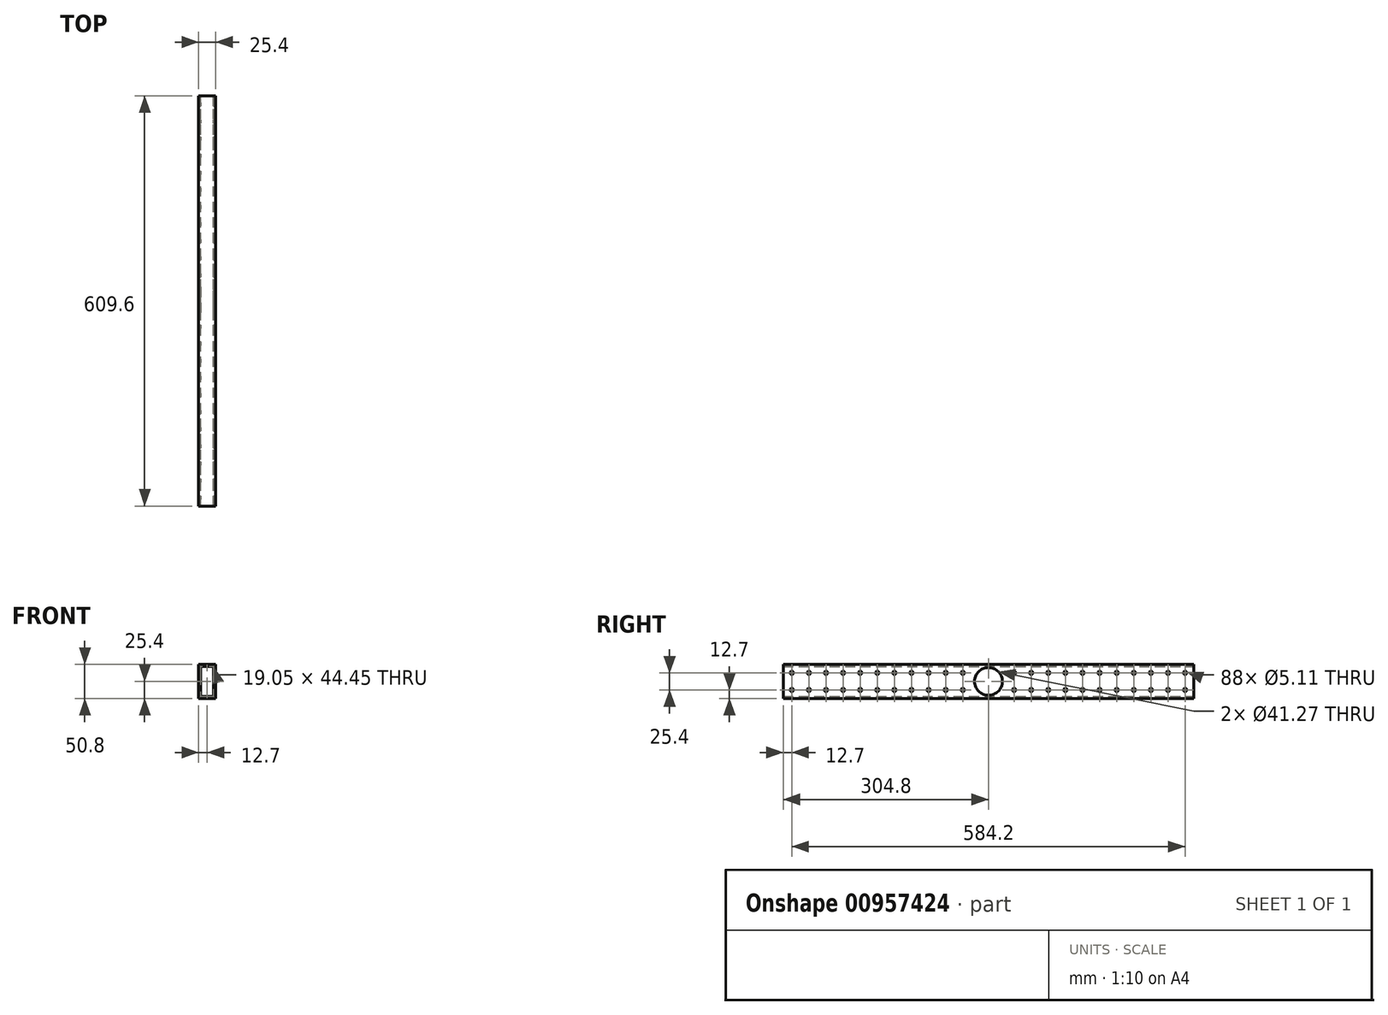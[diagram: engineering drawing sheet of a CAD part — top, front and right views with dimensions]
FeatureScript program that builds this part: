
annotation { "Feature Type Name" : "Feature", "Feature Type Description" : "" }
export const myFeature = defineFeature(function(context is Context, id is Id, definition is map)
    precondition{}
    {
        {
            var Q0;
            Q0=qCreatedBy(makeId("Front.planeOp"),FACE);
            var sketch = newSketch(context, id + "F0", { "sketchPlane" : qUnion([Q0])});
            skLineSegment(sketch, "E0.bottom", {"start": v(-12.7, 25.4) * mm, "end": v(12.7, 25.4) * mm});
            skLineSegment(sketch, "E0.top", {"start": v(-12.7, -25.4) * mm, "end": v(12.7, -25.4) * mm});
            skLineSegment(sketch, "E0.left", {"start": v(-12.7, 25.4) * mm, "end": v(-12.7, -25.4) * mm});
            skLineSegment(sketch, "E0.right", {"start": v(12.7, 25.4) * mm, "end": v(12.7, -25.4) * mm});
            skPoint(sketch, "E0.middle", {"position": v(0, 0) * mm});
            skLineSegment(sketch, "E1.0", {"start": v(-9.52, 22.22) * mm, "end": v(9.53, 22.22) * mm});
            skLineSegment(sketch, "E1.1", {"start": v(-9.52, 22.22) * mm, "end": v(-9.53, -22.23) * mm});
            skLineSegment(sketch, "E1.2", {"start": v(-9.53, -22.23) * mm, "end": v(9.53, -22.23) * mm});
            skLineSegment(sketch, "E1.3", {"start": v(9.53, 22.22) * mm, "end": v(9.53, -22.23) * mm});
            skSolve(sketch);
        }
        {
            var Q0;
            Q0 = qSketchRegion(id + "F0", true);
            extrude(context, id + "F1", {"entities" : qUnion([Q0]), "depth" : 609.6 * mm, "offsetDistance" : 25.4 * mm});
        }
        {
            var Q0;
            Q0=makeQuery(id+"F1.opExtrude","SWEPT_FACE",FACE,{"disambiguationData":[OSD([sQuery(id+"F0.wireOp",EDGE,"E0.right")])]});
            var sketch = newSketch(context, id + "F2", { "sketchPlane" : qUnion([Q0])});
            skCircle(sketch, "E2", {"center": v(-596.9, 12.7) * mm, "radius": 2.55 * mm});
            skCircle(sketch, "E3.0.1.0", {"center": v(-596.9, -12.7) * mm, "radius": 2.55 * mm});
            skCircle(sketch, "E3.1.0.0", {"center": v(-571.5, 12.7) * mm, "radius": 2.55 * mm});
            skCircle(sketch, "E3.1.1.0", {"center": v(-571.5, -12.7) * mm, "radius": 2.55 * mm});
            skCircle(sketch, "E3.2.0.0", {"center": v(-546.1, 12.7) * mm, "radius": 2.55 * mm});
            skCircle(sketch, "E3.2.1.0", {"center": v(-546.1, -12.7) * mm, "radius": 2.55 * mm});
            skCircle(sketch, "E3.3.0.0", {"center": v(-520.7, 12.7) * mm, "radius": 2.55 * mm});
            skCircle(sketch, "E3.3.1.0", {"center": v(-520.7, -12.7) * mm, "radius": 2.55 * mm});
            skCircle(sketch, "E3.4.0.0", {"center": v(-495.3, 12.7) * mm, "radius": 2.55 * mm});
            skCircle(sketch, "E3.4.1.0", {"center": v(-495.3, -12.7) * mm, "radius": 2.55 * mm});
            skCircle(sketch, "E3.5.0.0", {"center": v(-469.9, 12.7) * mm, "radius": 2.55 * mm});
            skCircle(sketch, "E3.5.1.0", {"center": v(-469.9, -12.7) * mm, "radius": 2.55 * mm});
            skCircle(sketch, "E3.6.0.0", {"center": v(-444.5, 12.7) * mm, "radius": 2.55 * mm});
            skCircle(sketch, "E3.6.1.0", {"center": v(-444.5, -12.7) * mm, "radius": 2.55 * mm});
            skCircle(sketch, "E3.7.0.0", {"center": v(-419.1, 12.7) * mm, "radius": 2.55 * mm});
            skCircle(sketch, "E3.7.1.0", {"center": v(-419.1, -12.7) * mm, "radius": 2.55 * mm});
            skCircle(sketch, "E3.8.0.0", {"center": v(-393.7, 12.7) * mm, "radius": 2.55 * mm});
            skCircle(sketch, "E3.8.1.0", {"center": v(-393.7, -12.7) * mm, "radius": 2.55 * mm});
            skCircle(sketch, "E3.9.0.0", {"center": v(-368.3, 12.7) * mm, "radius": 2.55 * mm});
            skCircle(sketch, "E3.9.1.0", {"center": v(-368.3, -12.7) * mm, "radius": 2.55 * mm});
            skCircle(sketch, "E3.10.0.0", {"center": v(-342.9, 12.7) * mm, "radius": 2.55 * mm});
            skCircle(sketch, "E3.10.1.0", {"center": v(-342.9, -12.7) * mm, "radius": 2.55 * mm});
            skCircle(sketch, "E3.11.0.0", {"center": v(-317.5, 12.7) * mm, "radius": 2.55 * mm});
            skCircle(sketch, "E3.11.1.0", {"center": v(-317.5, -12.7) * mm, "radius": 2.55 * mm});
            skCircle(sketch, "E3.12.0.0", {"center": v(-292.1, 12.7) * mm, "radius": 2.55 * mm});
            skCircle(sketch, "E3.12.1.0", {"center": v(-292.1, -12.7) * mm, "radius": 2.55 * mm});
            skCircle(sketch, "E3.13.0.0", {"center": v(-266.7, 12.7) * mm, "radius": 2.55 * mm});
            skCircle(sketch, "E3.13.1.0", {"center": v(-266.7, -12.7) * mm, "radius": 2.55 * mm});
            skCircle(sketch, "E3.14.0.0", {"center": v(-241.3, 12.7) * mm, "radius": 2.55 * mm});
            skCircle(sketch, "E3.14.1.0", {"center": v(-241.3, -12.7) * mm, "radius": 2.55 * mm});
            skCircle(sketch, "E3.15.0.0", {"center": v(-215.9, 12.7) * mm, "radius": 2.55 * mm});
            skCircle(sketch, "E3.15.1.0", {"center": v(-215.9, -12.7) * mm, "radius": 2.55 * mm});
            skCircle(sketch, "E3.16.0.0", {"center": v(-190.5, 12.7) * mm, "radius": 2.55 * mm});
            skCircle(sketch, "E3.16.1.0", {"center": v(-190.5, -12.7) * mm, "radius": 2.55 * mm});
            skCircle(sketch, "E3.17.0.0", {"center": v(-165.1, 12.7) * mm, "radius": 2.55 * mm});
            skCircle(sketch, "E3.17.1.0", {"center": v(-165.1, -12.7) * mm, "radius": 2.55 * mm});
            skCircle(sketch, "E3.18.0.0", {"center": v(-139.7, 12.7) * mm, "radius": 2.55 * mm});
            skCircle(sketch, "E3.18.1.0", {"center": v(-139.7, -12.7) * mm, "radius": 2.55 * mm});
            skCircle(sketch, "E3.19.0.0", {"center": v(-114.3, 12.7) * mm, "radius": 2.55 * mm});
            skCircle(sketch, "E3.19.1.0", {"center": v(-114.3, -12.7) * mm, "radius": 2.55 * mm});
            skCircle(sketch, "E3.20.0.0", {"center": v(-88.9, 12.7) * mm, "radius": 2.55 * mm});
            skCircle(sketch, "E3.20.1.0", {"center": v(-88.9, -12.7) * mm, "radius": 2.55 * mm});
            skCircle(sketch, "E3.21.0.0", {"center": v(-63.5, 12.7) * mm, "radius": 2.55 * mm});
            skCircle(sketch, "E3.21.1.0", {"center": v(-63.5, -12.7) * mm, "radius": 2.55 * mm});
            skCircle(sketch, "E3.22.0.0", {"center": v(-38.1, 12.7) * mm, "radius": 2.55 * mm});
            skCircle(sketch, "E3.22.1.0", {"center": v(-38.1, -12.7) * mm, "radius": 2.55 * mm});
            skCircle(sketch, "E3.23.0.0", {"center": v(-12.7, 12.7) * mm, "radius": 2.55 * mm});
            skCircle(sketch, "E3.23.1.0", {"center": v(-12.7, -12.7) * mm, "radius": 2.55 * mm});
            skLineSegment(sketch, "E3.direction1", {"start": v(-596.9, 12.7) * mm, "end": v(-571.5, 12.7) * mm, "construction": true});
            skLineSegment(sketch, "E3.direction2", {"start": v(-596.9, 12.7) * mm, "end": v(-596.9, -12.7) * mm, "construction": true});
            skSolve(sketch);
        }
        {
            var Q0;
            Q0 = qSketchRegion(id + "F2", true);
            extrude(context, id + "F3", {"entities" : qUnion([Q0]), "operationType" : NewBodyOperationType.REMOVE, "oppositeDirection" : true, "depth" : 25.4 * mm, "offsetDistance" : 25.4 * mm});
        }
        {
            var Q0;
            Q0=makeQuery(id+"F1.opExtrude","SWEPT_FACE",FACE,{"disambiguationData":[OSD([sQuery(id+"F0.wireOp",EDGE,"E0.right")])]});
            var sketch = newSketch(context, id + "F4", { "sketchPlane" : qUnion([Q0])});
            skCircle(sketch, "E4", {"center": v(-304.8, 0) * mm, "radius": 20.64 * mm});
            skPoint(sketch, "E4.centerSnap0", {"position": v(-304.8, 25.4) * mm});
            skSolve(sketch);
        }
        {
            var Q0;
            Q0 = qSketchRegion(id + "F4", true);
            extrude(context, id + "F5", {"entities" : qUnion([Q0]), "operationType" : NewBodyOperationType.REMOVE, "oppositeDirection" : true, "depth" : 25.4 * mm, "offsetDistance" : 25.4 * mm});
        }
    });
